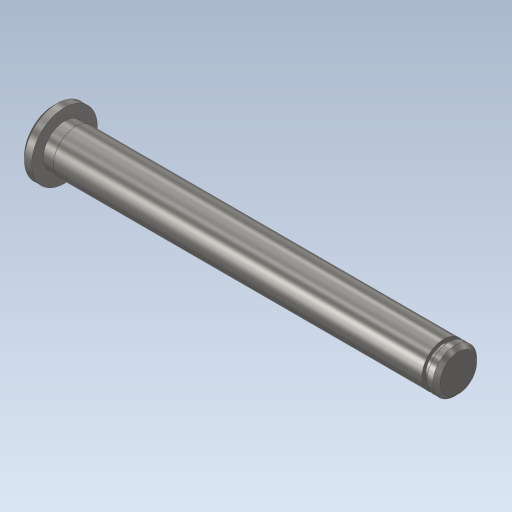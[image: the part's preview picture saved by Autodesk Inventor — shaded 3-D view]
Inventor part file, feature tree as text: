
AUTODESK INVENTOR PART (.ipt)
format: ipt  version: 2024 (Build 280153000, 153)  size: 196,096 bytes
history: native  units: mm
features: other x21, revolve x1, sketch x1
ambient origin geometry x8: Origin, YZ Plane, XZ Plane, XY Plane, X Axis, Y Axis, Z Axis, Center Point
bodies: Solid1 (feature_tree)
feature tree (23):
  revolve  "Revolution1"  [1 undecoded]
  other  "pin_to_body_XY"
  other  "pin_to_body_YZ"
  other  "pin_to_body_ZX"
  other  "pin_to_body_X"
  other  "pin_to_body_Y"
  other  "pin_to_body_Z"
  other  "pin_to_body_Center"
  other  "pin_to_knuckle_XY"
  other  "pin_to_knuckle_YZ"
  other  "pin_to_knuckle_ZX"
  other  "pin_to_knuckle_X"
  other  "pin_to_knuckle_Y"
  other  "pin_to_knuckle_Z"
  other  "pin_to_knuckle_Center"
  other  "pin_to_rring_XY"
  other  "pin_to_rring_YZ"
  other  "pin_to_rring_ZX"
  other  "pin_to_rring_X"
  other  "pin_to_rring_Y"
  other  "pin_to_rring_Z"
  other  "pin_to_rring_Center"
  sketch  "Sketch_1"  dims[d0=360.0deg d1=0.0mm]
note: 1 required parameter value undecoded (feature->parameter linkage not recoverable at this tier; creation-order binding heuristic only, values carry confidence <= 0.55)
